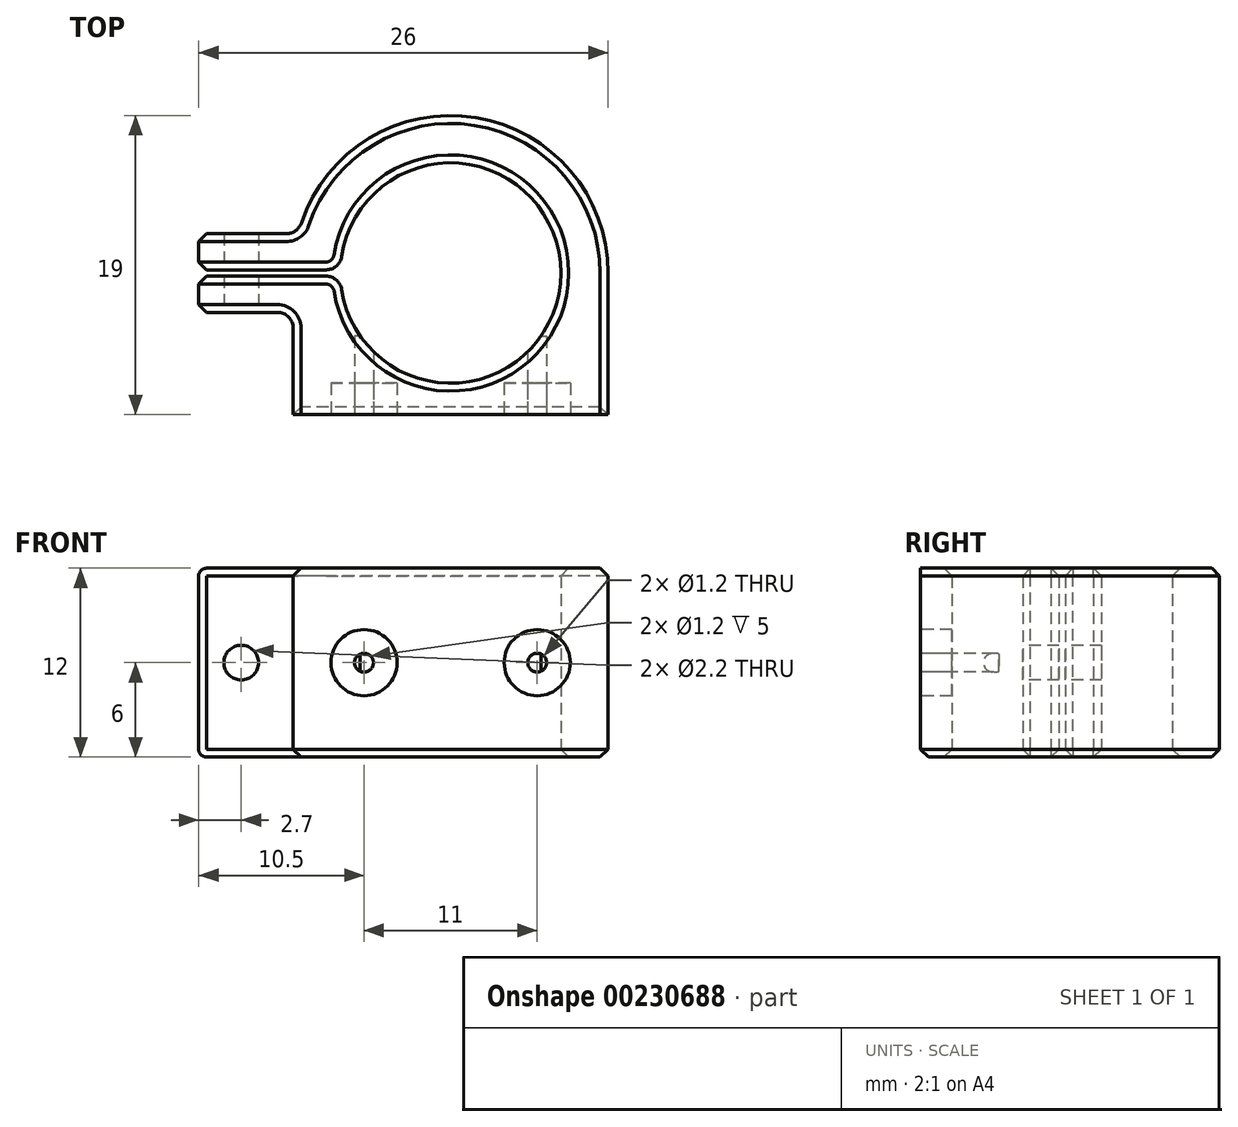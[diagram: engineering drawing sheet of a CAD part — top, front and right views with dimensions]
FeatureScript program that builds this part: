
annotation { "Feature Type Name" : "Feature", "Feature Type Description" : "" }
export const myFeature = defineFeature(function(context is Context, id is Id, definition is map)
    precondition{}
    {
        {
            var Q0;
            Q0=qCreatedBy(makeId("Top.planeOp"),FACE);
            var sketch = newSketch(context, id + "F0", { "sketchPlane" : qUnion([Q0])});
            skLineSegment(sketch, "E0.top", {"start": v(-10, -9) * mm, "end": v(10, -9) * mm});
            skLineSegment(sketch, "E0.left", {"start": v(-10, -3.5) * mm, "end": v(-10, -9) * mm});
            skLineSegment(sketch, "E0.right", {"start": v(10, 0) * mm, "end": v(10, -9) * mm});
            skArc(sketch, "E1", {"start": v(-6.92, -1.05) * mm, "mid": v(7, 0) * mm, "end": v(-6.92, 1.05) * mm});
            skArc(sketch, "E2.0", {"start": v(10, 0) * mm, "mid": v(1.61, 9.87) * mm, "end": v(-9.48, 3.18) * mm});
            skLineSegment(sketch, "E3.bottom", {"start": v(-16, 2.5) * mm, "end": v(-10.43, 2.5) * mm});
            skLineSegment(sketch, "E3.top", {"start": v(-16, -2.5) * mm, "end": v(-11, -2.5) * mm});
            skLineSegment(sketch, "E3.left", {"start": v(-16, 2.5) * mm, "end": v(-16, 0.2) * mm});
            skPoint(sketch, "E4.orphan", {"position": v(-10, 0) * mm});
            skPoint(sketch, "E5.visualSharp", {"position": v(-9.68, 2.5) * mm});
            skArc(sketch, "E5.filletArc", {"start": v(-10.43, 2.5) * mm, "mid": v(-9.84, 2.69) * mm, "end": v(-9.48, 3.18) * mm});
            skPoint(sketch, "E6.visualSharp", {"position": v(-10, -2.5) * mm});
            skArc(sketch, "E6.filletArc", {"start": v(-10, -3.5) * mm, "mid": v(-10.3, -2.8) * mm, "end": v(-11, -2.5) * mm});
            skLineSegment(sketch, "E7.0", {"start": v(-7.9, 0.2) * mm, "end": v(-16, 0.2) * mm});
            skLineSegment(sketch, "E8.0", {"start": v(-7.9, -0.2) * mm, "end": v(-16, -0.2) * mm});
            skLineSegment(sketch, "E9.trimOffspring", {"start": v(-16, -0.2) * mm, "end": v(-16, -2.5) * mm});
            skPoint(sketch, "E10.visualSharp", {"position": v(-7, 0.2) * mm});
            skArc(sketch, "E10.filletArc", {"start": v(-7.9, 0.2) * mm, "mid": v(-7.26, 0.44) * mm, "end": v(-6.92, 1.05) * mm});
            skPoint(sketch, "E11.visualSharp", {"position": v(-7, -0.2) * mm});
            skArc(sketch, "E11.filletArc", {"start": v(-6.92, -1.05) * mm, "mid": v(-7.26, -0.44) * mm, "end": v(-7.9, -0.2) * mm});
            skSolve(sketch);
        }
        {
            var Q0;
            Q0=qSketchRegion(id+"F0",true);
            extrude(context, id + "F1", {"entities" : qUnion([Q0]), "depth" : 12 * mm});
        }
        {
            var Q0;
            Q0=makeQuery(id+"F1.opExtrude","SWEPT_FACE",FACE,{"disambiguationData":[OSD([sQuery(id+"F0.wireOp",EDGE,"E0.top")])]});
            var sketch = newSketch(context, id + "F2", { "sketchPlane" : qUnion([Q0])});
            skCircle(sketch, "E12", {"center": v(-5.5, 6) * mm, "radius": 0.6 * mm});
            skCircle(sketch, "E13.MirrorC", {"center": v(5.5, 6) * mm, "radius": 0.6 * mm});
            skSolve(sketch);
        }
        {
            var Q0;
            Q0=qSketchRegion(id+"F2",true);
            extrude(context, id + "F3", {"entities" : qUnion([Q0]), "operationType" : NewBodyOperationType.REMOVE, "oppositeDirection" : true, "depth" : 5 * mm});
        }
        {
            var Q0;
            Q0=makeQuery(id+"F1.opExtrude","SWEPT_FACE",FACE,{"disambiguationData":[OSD([sQuery(id+"F0.wireOp",EDGE,"E0.top")])]});
            var sketch = newSketch(context, id + "F4", { "sketchPlane" : qUnion([Q0])});
            skCircle(sketch, "E14.0", {"center": v(-5.5, 6) * mm, "radius": 2.1 * mm});
            skCircle(sketch, "E15.0", {"center": v(5.5, 6) * mm, "radius": 2.1 * mm});
            skCircle(sketch, "E16.0", {"center": v(-5.5, 6) * mm, "radius": 0.6 * mm});
            skCircle(sketch, "E17.0", {"center": v(5.5, 6) * mm, "radius": 0.6 * mm});
            skSolve(sketch);
        }
        {
            var Q0;
            Q0=makeQuery(id+"F4.imprint","IMPRINT",FACE,{"disambiguationData":[TD([[makeQuery(id+"F4.imprint","IMPRINT",EDGE,{"derivedFrom":sQuery(id+"F4.wireOp",EDGE,"E15.0")}),1.0]])]});
            var Q1;
            Q1=makeQuery(id+"F4.imprint","IMPRINT",FACE,{"disambiguationData":[TD([[makeQuery(id+"F4.imprint","IMPRINT",EDGE,{"derivedFrom":sQuery(id+"F4.wireOp",EDGE,"E14.0")}),1.0]])]});
            extrude(context, id + "F5", {"entities" : qUnion([Q0, Q1]), "flatOperationType" : FlatOperationType.REMOVE, "oppositeDirection" : true, "offsetDistance" : 25 * mm, "depth" : 2 * mm, "domain" : OperationDomain.MODEL});
        }
        {
            var Q0;
            Q0=makeQuery(id+"F1.opExtrude","SWEPT_FACE",FACE,{"disambiguationData":[OSD([sQuery(id+"F0.wireOp",EDGE,"E3.top")])]});
            var sketch = newSketch(context, id + "F6", { "sketchPlane" : qUnion([Q0])});
            skCircle(sketch, "E18", {"center": v(-13.3, 6) * mm, "radius": 1.1 * mm});
            skSolve(sketch);
        }
        {
            var Q0;
            Q0=qSketchRegion(id+"F6",true);
            extrude(context, id + "F7", {"entities" : qUnion([Q0]), "operationType" : NewBodyOperationType.REMOVE, "oppositeDirection" : true, "depth" : 25 * mm});
        }
        {
            var Q0;
            Q0=makeQuery(id+"F1.opExtrude","CAP_EDGE",EDGE,{"disambiguationData":[OSD([sQuery(id+"F0.wireOp",EDGE,"E3.left")])],"isStart":true});
            var Q1;
            Q1=makeQuery(id+"F1.opExtrude","CAP_EDGE",EDGE,{"disambiguationData":[OSD([sQuery(id+"F0.wireOp",EDGE,"E9.trimOffspring")])],"isStart":true});
            var Q2;
            Q2=makeQuery(id+"F1.opExtrude","CAP_EDGE",EDGE,{"disambiguationData":[OSD([sQuery(id+"F0.wireOp",EDGE,"E9.trimOffspring")])],"isStart":false});
            var Q3;
            Q3=makeQuery(id+"F1.opExtrude","CAP_EDGE",EDGE,{"disambiguationData":[OSD([sQuery(id+"F0.wireOp",EDGE,"E3.left")])],"isStart":false});
            fillet(context, id + "F8", {"entities" : qUnion([Q0, Q1, Q2, Q3]), "radius" : 0.5 * mm, "tangentPropagation" : true, "allowEdgeOverflow" : false});
        }
        {
            var Q0;
            Q0=makeQuery(id+"F1.opExtrude","CAP_EDGE",EDGE,{"disambiguationData":[OSD([sQuery(id+"F0.wireOp",EDGE,"E1")])],"isStart":true});
            var Q1;
            Q1=makeQuery(id+"F1.opExtrude","CAP_EDGE",EDGE,{"disambiguationData":[OSD([sQuery(id+"F0.wireOp",EDGE,"E2.0")])],"isStart":true});
            var Q2;
            Q2=makeQuery(id+"F1.opExtrude","CAP_EDGE",EDGE,{"disambiguationData":[OSD([sQuery(id+"F0.wireOp",EDGE,"E0.top")])],"isStart":true});
            var Q3;
            Q3=makeQuery(id+"F1.opExtrude","CAP_EDGE",EDGE,{"disambiguationData":[OSD([sQuery(id+"F0.wireOp",EDGE,"E0.left")])],"isStart":true});
            chamfer(context, id + "F9", {"entities" : qUnion([Q0, Q1, Q2, Q3]), "width" : 0.5 * mm, "tangentPropagation" : true});
        }
    });
